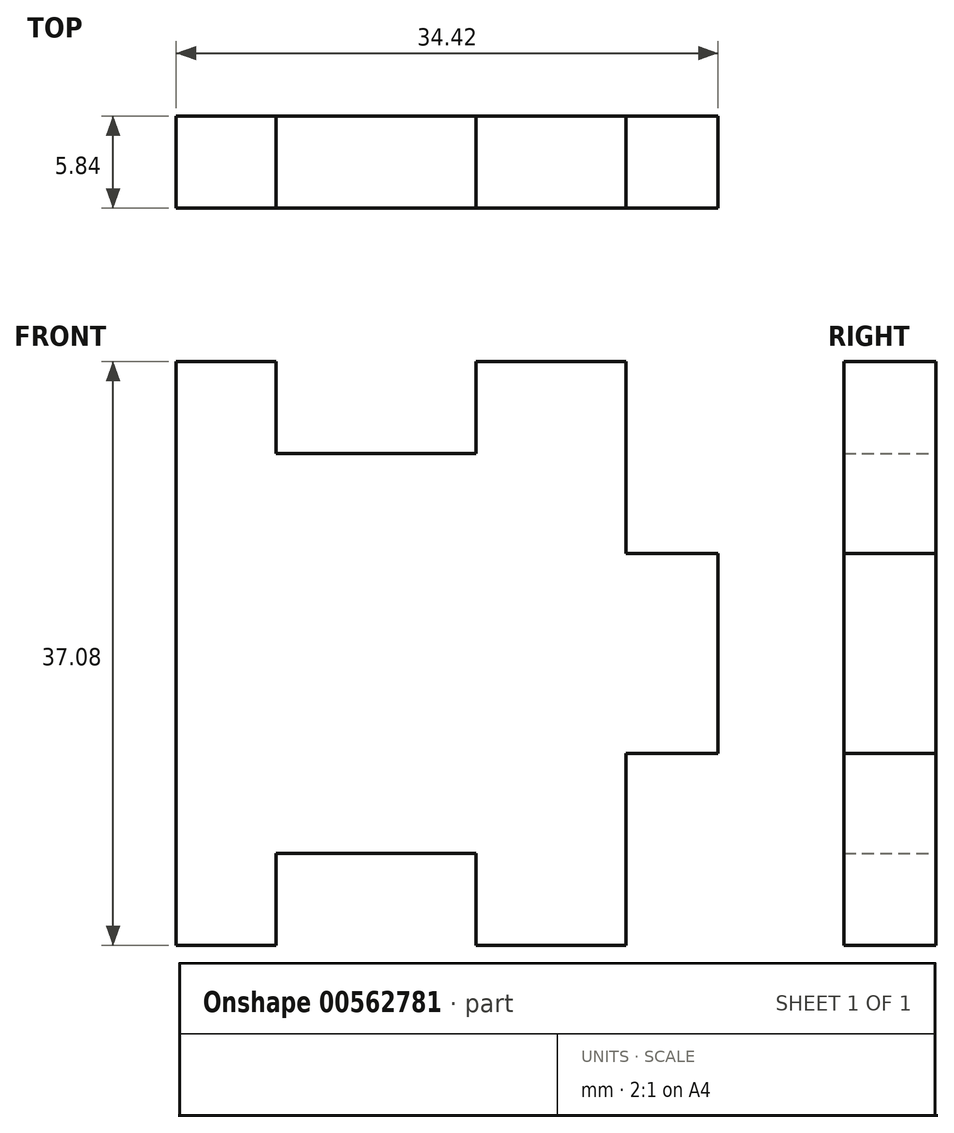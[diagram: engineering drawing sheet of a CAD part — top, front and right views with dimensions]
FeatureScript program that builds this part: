
annotation { "Feature Type Name" : "Feature", "Feature Type Description" : "" }
export const myFeature = defineFeature(function(context is Context, id is Id, definition is map)
    precondition{}
    {
        {
            var Q0;
            Q0=qCreatedBy(makeId("Front.planeOp"),FACE);
            var sketch = newSketch(context, id + "F0", { "sketchPlane" : qUnion([Q0])});
            skLineSegment(sketch, "E0.bottom", {"start": v(4.76, 12.7) * mm, "end": v(-7.94, 12.7) * mm});
            skLineSegment(sketch, "E0.top", {"start": v(4.76, -12.7) * mm, "end": v(-7.94, -12.7) * mm});
            skLineSegment(sketch, "E0.left", {"start": v(14.29, 12.7) * mm, "end": v(14.29, 6.35) * mm});
            skLineSegment(sketch, "E0.right", {"start": v(-14.29, 12.7) * mm, "end": v(-14.29, -12.7) * mm});
            skPoint(sketch, "E0.middle", {"position": v(0, 0) * mm});
            skLineSegment(sketch, "E1.bottom", {"start": v(14.29, 6.35) * mm, "end": v(20.13, 6.35) * mm});
            skLineSegment(sketch, "E1.top", {"start": v(14.29, -6.35) * mm, "end": v(20.13, -6.35) * mm});
            skLineSegment(sketch, "E1.right", {"start": v(20.13, 6.35) * mm, "end": v(20.13, -6.35) * mm});
            skPoint(sketch, "E1.middle", {"position": v(17.2, 0) * mm});
            skLineSegment(sketch, "E2.top", {"start": v(-14.29, 18.54) * mm, "end": v(-7.94, 18.54) * mm});
            skLineSegment(sketch, "E2.left", {"start": v(-14.29, 12.7) * mm, "end": v(-14.29, 18.54) * mm});
            skLineSegment(sketch, "E2.right", {"start": v(-7.94, 12.7) * mm, "end": v(-7.94, 18.54) * mm});
            skPoint(sketch, "E2.middle", {"position": v(-11.11, 15.62) * mm});
            skLineSegment(sketch, "E3.top", {"start": v(4.76, 18.54) * mm, "end": v(14.29, 18.54) * mm});
            skLineSegment(sketch, "E3.left", {"start": v(4.76, 12.7) * mm, "end": v(4.76, 18.54) * mm});
            skLineSegment(sketch, "E3.right", {"start": v(14.29, 12.7) * mm, "end": v(14.29, 18.54) * mm});
            skPoint(sketch, "E3.middle", {"position": v(9.52, 15.62) * mm});
            skLineSegment(sketch, "E4.trimOffspring", {"start": v(14.29, -6.35) * mm, "end": v(14.29, -12.7) * mm});
            skLineSegment(sketch, "E5.MirrorCS", {"start": v(4.76, -12.7) * mm, "end": v(4.76, -18.54) * mm});
            skLineSegment(sketch, "E6.MirrorCS", {"start": v(4.76, -18.54) * mm, "end": v(14.29, -18.54) * mm});
            skLineSegment(sketch, "E7.MirrorCS", {"start": v(-7.94, -12.7) * mm, "end": v(-7.94, -18.54) * mm});
            skLineSegment(sketch, "E8.MirrorCS", {"start": v(-14.29, -12.7) * mm, "end": v(-14.29, -18.54) * mm});
            skLineSegment(sketch, "E9.MirrorCS", {"start": v(-14.29, -18.54) * mm, "end": v(-7.94, -18.54) * mm});
            skPoint(sketch, "E10.MirrorP", {"position": v(-11.11, -15.62) * mm});
            skLineSegment(sketch, "E11.MirrorCS", {"start": v(14.29, -12.7) * mm, "end": v(14.29, -18.54) * mm});
            skPoint(sketch, "E12.MirrorP", {"position": v(9.52, -15.62) * mm});
            skSolve(sketch);
        }
        {
            var Q0;
            Q0 = qSketchRegion(id + "F0", true);
            extrude(context, id + "F1", {"entities" : qUnion([Q0]), "depth" : 5.84 * mm, "offsetDistance" : 25.4 * mm});
        }
    });
